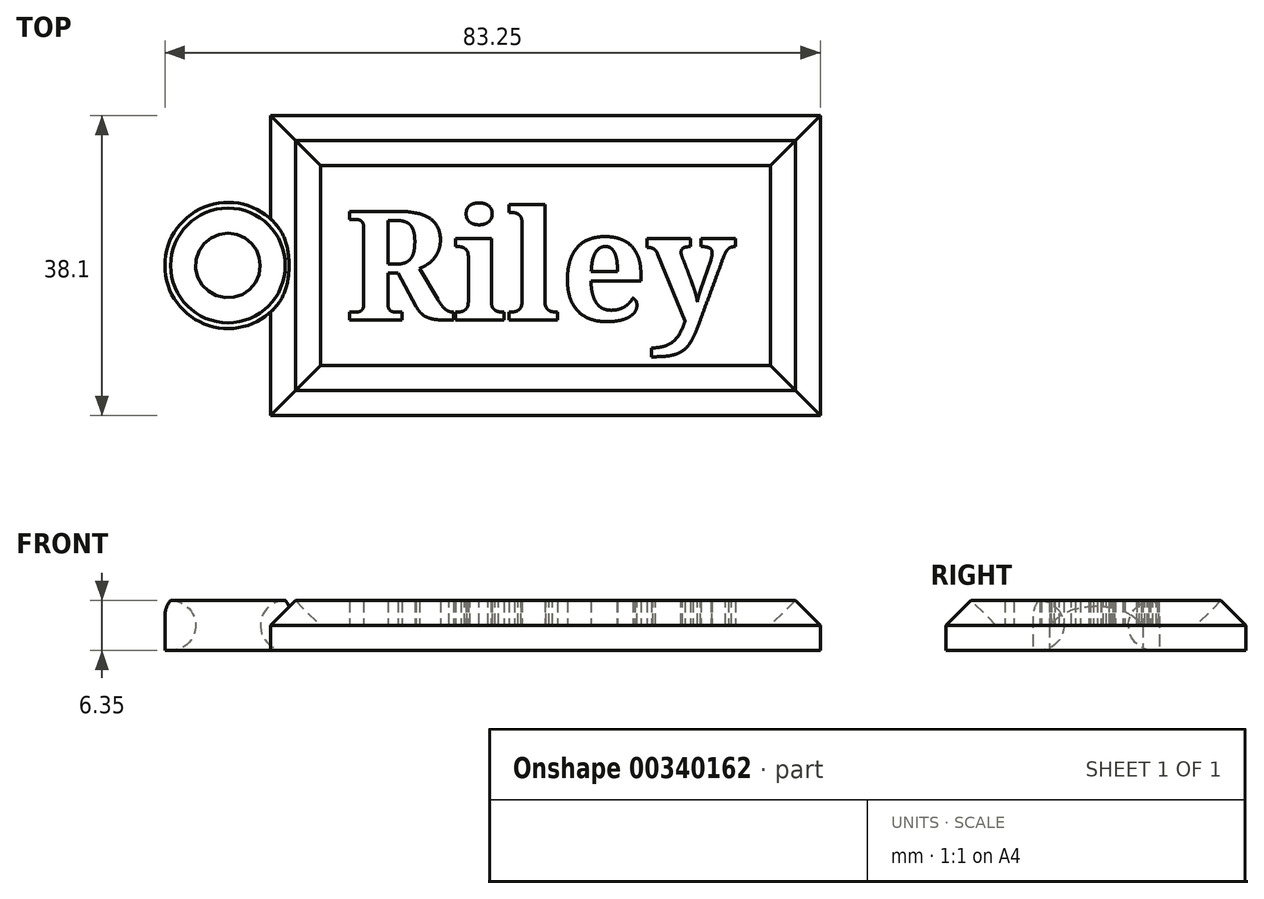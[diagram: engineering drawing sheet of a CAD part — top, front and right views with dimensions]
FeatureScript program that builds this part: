
annotation { "Feature Type Name" : "Feature", "Feature Type Description" : "" }
export const myFeature = defineFeature(function(context is Context, id is Id, definition is map)
    precondition{}
    {
        {
            var Q0;
            Q0=qCreatedBy(makeId("Top.planeOp"),FACE);
            var sketch = newSketch(context, id + "F0", { "sketchPlane" : qUnion([Q0])});
            skLineSegment(sketch, "E0.bottom", {"start": v(0, 38.1) * mm, "end": v(69.85, 38.1) * mm});
            skLineSegment(sketch, "E0.top", {"start": v(0, 0) * mm, "end": v(69.85, 0) * mm});
            skLineSegment(sketch, "E0.left", {"start": v(0, 38.1) * mm, "end": v(0, 0) * mm});
            skLineSegment(sketch, "E0.right", {"start": v(69.85, 38.1) * mm, "end": v(69.85, 0) * mm});
            skSolve(sketch);
        }
        {
            var Q0;
            Q0 = qSketchRegion(id + "F0", true);
            extrude(context, id + "F1", {"entities" : qUnion([Q0]), "depth" : 3.17 * mm});
        }
        {
            var Q0;
            Q0=makeQuery(id+"F1.opExtrude","CAP_FACE",FACE,{"disambiguationData":[OSD([sQuery(id+"F0.wireOp",EDGE,"E0.bottom"),sQuery(id+"F0.wireOp",EDGE,"E0.top"),sQuery(id+"F0.wireOp",EDGE,"E0.left"),sQuery(id+"F0.wireOp",EDGE,"E0.right")])],"isStart":false});
            var sketch = newSketch(context, id + "F2", { "sketchPlane" : qUnion([Q0])});
            skLineSegment(sketch, "E1.bottom", {"start": v(63.5, 6.35) * mm, "end": v(6.35, 6.35) * mm});
            skLineSegment(sketch, "E1.top", {"start": v(63.5, 31.75) * mm, "end": v(6.35, 31.75) * mm});
            skLineSegment(sketch, "E1.left", {"start": v(63.5, 6.35) * mm, "end": v(63.5, 31.75) * mm});
            skLineSegment(sketch, "E1.right", {"start": v(6.35, 6.35) * mm, "end": v(6.35, 31.75) * mm});
            skSolve(sketch);
        }
        {
            var Q0;
            Q0=makeQuery(id+"F2.imprint","IMPRINT",FACE,{"disambiguationData":[TD([[makeQuery(id+"F2.imprint","IMPRINT",EDGE,{"derivedFrom":sQuery(id+"F2.wireOp",EDGE,"E1.bottom")}),1.0]])]});
            extrude(context, id + "F3", {"entities" : qUnion([Q0]), "operationType" : NewBodyOperationType.ADD, "depth" : 3.17 * mm});
        }
        {
            var Q0;
            Q0=makeQuery(id+"F3.opExtrude","CAP_EDGE",EDGE,{"disambiguationData":[OSD([sQuery(id+"F0.wireOp",EDGE,"E0.left")])],"isStart":false});
            var Q1;
            Q1=makeQuery(id+"F3.opExtrude","CAP_EDGE",EDGE,{"disambiguationData":[OSD([sQuery(id+"F0.wireOp",EDGE,"E0.bottom")])],"isStart":false});
            var Q2;
            Q2=makeQuery(id+"F3.opExtrude","CAP_EDGE",EDGE,{"disambiguationData":[OSD([sQuery(id+"F0.wireOp",EDGE,"E0.top")])],"isStart":false});
            var Q3;
            Q3=makeQuery(id+"F3.opExtrude","CAP_EDGE",EDGE,{"disambiguationData":[OSD([sQuery(id+"F2.wireOp",EDGE,"E1.right")])],"isStart":false});
            var Q4;
            Q4=makeQuery(id+"F3.opExtrude","CAP_EDGE",EDGE,{"disambiguationData":[OSD([sQuery(id+"F2.wireOp",EDGE,"E1.bottom")])],"isStart":false});
            var Q5;
            Q5=makeQuery(id+"F3.opExtrude","CAP_EDGE",EDGE,{"disambiguationData":[OSD([sQuery(id+"F2.wireOp",EDGE,"E1.top")])],"isStart":false});
            var Q6;
            Q6=makeQuery(id+"F3.opExtrude","CAP_EDGE",EDGE,{"disambiguationData":[OSD([sQuery(id+"F0.wireOp",EDGE,"E0.right")])],"isStart":false});
            var Q7;
            Q7=makeQuery(id+"F3.opExtrude","CAP_EDGE",EDGE,{"disambiguationData":[OSD([sQuery(id+"F2.wireOp",EDGE,"E1.left")])],"isStart":false});
            chamfer(context, id + "F4", {"entities" : qUnion([Q0, Q1, Q2, Q3, Q4, Q5, Q6, Q7]), "width" : 3.17 * mm, "tangentPropagation" : true});
        }
        {
            var Q0;
            Q0=makeQuery(id+"F1.opExtrude","CAP_FACE",FACE,{"disambiguationData":[OSD([sQuery(id+"F0.wireOp",EDGE,"E0.bottom"),sQuery(id+"F0.wireOp",EDGE,"E0.top"),sQuery(id+"F0.wireOp",EDGE,"E0.left"),sQuery(id+"F0.wireOp",EDGE,"E0.right")])],"isStart":false});
            var sketch = newSketch(context, id + "F5", { "sketchPlane" : qUnion([Q0])});
            skText(sketch, "E2", { "text": "Riley", "fontName": "NotoSerif-Bold.ttf"});
            const initialGuessF5  = {"E2": [0.00953, 0.0121, 1, 0, 0.01393]};
            skSetInitialGuess(sketch, initialGuessF5);
            skSolve(sketch);
        }
        {
            var Q0;
            Q0 = qSketchRegion(id + "F5", true);
            extrude(context, id + "F6", {"entities" : qUnion([Q0]), "operationType" : NewBodyOperationType.ADD, "depth" : 3.17 * mm});
        }
        {
            var Q0;
            Q0=qCreatedBy(makeId("Top.planeOp"),FACE);
            var sketch = newSketch(context, id + "F7", { "sketchPlane" : qUnion([Q0])});
            skCircle(sketch, "E3", {"center": v(-5.38, 19.05) * mm, "radius": 8.02 * mm});
            skCircle(sketch, "E4", {"center": v(-5.38, 19.05) * mm, "radius": 4.1 * mm});
            skSolve(sketch);
        }
        {
            var Q0;
            Q0 = qSketchRegion(id + "F7", true);
            extrude(context, id + "F8", {"entities" : qUnion([Q0]), "operationType" : NewBodyOperationType.ADD, "depth" : 6.35 * mm});
        }
        {
            var Q0;
            Q0=makeQuery(id+"F8.opExtrude","CAP_EDGE",EDGE,{"disambiguationData":[OSD([sQuery(id+"F7.wireOp",EDGE,"E4")])],"isStart":false});
            fillet(context, id + "F9", {"entities" : qUnion([Q0]), "radius" : 3.17 * mm, "tangentPropagation" : true, "allowEdgeOverflow" : false});
        }
        {
            var Q0;
            Q0=makeQuery(id+"F8.opExtrude","CAP_EDGE",EDGE,{"disambiguationData":[OSD([sQuery(id+"F7.wireOp",EDGE,"E4")])],"isStart":true});
            fillet(context, id + "F10", {"entities" : qUnion([Q0]), "radius" : 3.17 * mm, "tangentPropagation" : true, "allowEdgeOverflow" : false});
        }
        {
            var Q0;
            Q0=makeQuery(id+"F8.opExtrude","CAP_EDGE",EDGE,{"disambiguationData":[OSD([sQuery(id+"F7.wireOp",EDGE,"E3")])],"isStart":false});
            fillet(context, id + "F11", {"entities" : qUnion([Q0]), "radius" : 3.17 * mm, "tangentPropagation" : true, "allowEdgeOverflow" : false});
        }
    });
